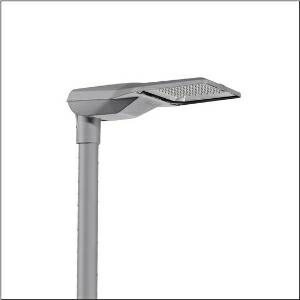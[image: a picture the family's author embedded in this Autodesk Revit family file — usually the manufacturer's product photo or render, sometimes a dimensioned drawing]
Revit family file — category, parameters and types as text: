
# Revit family: streetlight_sl_21_iq_midi___p0_5a_5xe3v31d08mb_1276
name_source: partatom
category: Lighting Fixtures
units: mm (PartAtom-declared; Revit-internal decimal feet)

## family parameters
Cut with Voids When Loaded = No
Host = Face
Light Source = No
Part Type = Normal
Room Calculation Point = No
Round Connector Dimension = Use Diameter
Shared = No

## types (1)
- --- (1 x LED, 19170 lm, 146.7 W, 3000K)
    Apparent Load = 147 VA
    CIE Flux Codes = 37 73 96 100 100
    Color Rendering = 70
    Color Temperature = 3000K
    Default Elevation = 1800 mm
    Description = Streetlight SL 21 iQ midi, mast luminaire, primary light control with lens, of PMMA, primary optical cover: cover, of toughened safety glass, transparent, light distribution: P0.5a, light emission: direct distribution, primary light characteristic: asymmetric, installation type: post-top, side-entry, LED, High Power LED, rated luminous flux: 19.170lm, luminous efficacy: 131lm/W, light colour: 730, colour temperature: 3000K, control gear: iQ-Comfort, control: pre-setting: linear dimming characteristic, Auto-Match, Temp-Guard, Lumen-Switch, Night-Set, Smart-Wire, Light-Fading, Desk-Remote (wireless, voltage-free reading and setting of iQ features in the workshop via application-optimized NFC function/RFID function), optimised constant luminous flux control (CLO 2.0), mains connection: 230..240V, AC, 50/60Hz, start of lifetime: 147W, end of service life: 161W, reduction: 62W, luminaire housing, of diecast aluminium, powder-coated, SITECO metallic grey (DB 702S), corrosivity category C5 high according to DIN EN ISO 12944, please order mast flange separately, inclination adjustable: 0°, 5°, 10°, 15°, sealing non-destructively replaceable, multi-level sealing system, length: 644mm, width: 335mm, height: 110mm, mast flange for spigot size: 42mm (side-entry): 5XC10008XM4, 60/48mm (side-entry/post-top): 5XC10108XM2, 76/60mm (side-entry/post-top): 5XC10108XM1, mounting height: 4..8m, protection rating (complete): IP66, insulation class (complete): insulation class II (safety insulation), certification: CE, ENEC, ENEC+, VDE, impact resistance: IK10, permissible operating ambient temperature for outdoor applications: -40..+50°C, standard-compliant lighting for roads and squares, packaging unit: 1 piece

Light Distribution: P0.5a
    Height = 111 mm
    Lamp = 1 x LED
    Lamp Light Flux = 19170 lm
    Lamp Power = 146.7 W
    Lamp count = 1
    Length = 644 mm
    Luminous efficacy = 131 lm/W
    Manufacturer = Siteco
    ModVariant = No
    Model = 5XE3V31D08MB
    Number of Poles = 1
    OnlyDefault = Yes
    Power Factor = 1
    Product Name = Streetlight SL 21 iQ midi | P0.5a
    Product group = mast luminaire | pylon top
    ProductGroupID = 6100
    Protection Class = Protection class II
    Protection Degree = IP 66
    RLX_Detail_Level = 1
    RLX_Emergency_Light_Flux = 0 lm
    RLX_Emergency_Type = 0
    RLX_Emergency_Type_DB = No
    RlxData = <blob elided: 90497 chars, md5=34786ad7>
    Socket = socket
    Standby Power = 0 W
    System Light Flux = 19169 lm
    System Power = 147 W
    Type Comments = factory setting: luminous flux: 100 % | dim-lin: 254 | 753 mA
    Type Image = l_1004298.jpg
    URL = http://relux.com
    VarID = @adj_077395
    Voltage = 0 V
    Weight = 0.00 kg
    Width = 336 mm

## geometry (parser evidence)
native form markers: Blend x4, Sweep x11
no freeform markers — native parametric forms only
